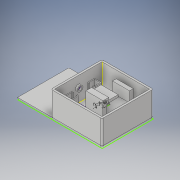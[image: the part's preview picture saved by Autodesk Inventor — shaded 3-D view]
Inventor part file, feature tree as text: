
AUTODESK INVENTOR PART (.ipt)
format: ipt  version: 2019 (Build 230136000, 136)  size: 371,712 bytes
history: native  units: in
note: dims shown in document units (in); Inventor stores cm internally (conversion verified against a paired STEP export)
features: extrude x25, sketch x22, fillet x2, other x1
ambient origin geometry x8: Origin, YZ Plane, XZ Plane, XY Plane, X Axis, Y Axis, Z Axis, Center Point
bodies: Solid1 (feature_tree)
feature tree (50):
  other  "ohisje"
  extrude  "Extrusion1"  Depth=1.9685in
  extrude  "Extrusion2"  Depth=0.0787in
  fillet  "Fillet1"  Radius=0.0787in
  sketch  "Sketch3"  dims[d5=0.0787in d6=1.378in]
  extrude  "Extrusion3"  Depth=1.378in
  sketch  "Sketch4"  dims[d7=2.126in d8=1.063in d9=0.0in d10=0.0787in]
  extrude  "Extrusion4"  Depth=1.063in TaperAngle=0.0deg
  fillet  "Fillet2"  Radius=0.0787in
  extrude  "Extrusion5"  Depth=0.0787in
  extrude  "Extrusion6"  Depth=0.315in
  extrude  "Extrusion7"  Depth=0.2402in
  sketch  "Sketch8"  dims[d30=0.0374in d31=0.0374in]
  extrude  "Extrusion8"  Depth=0.0374in
  extrude  "Extrusion9"  Depth=0.9843in
  extrude  "Extrusion10"  Depth=0.5906in TaperAngle=0.0deg
  extrude  "Extrusion11"  Depth=0.0394in
  extrude  "Extrusion12"  Depth=0.9843in
  sketch  "Sketch14"  dims[d46=0.1181in d47=1.2598in]
  extrude  "Extrusion13"  Depth=0.0394in TaperAngle=0.0deg
  extrude  "Extrusion14"  Depth=1.2598in
  extrude  "Extrusion16"  Depth=0.5512in TaperAngle=0.0deg
  extrude  "Extrusion17"  Depth=0.5512in TaperAngle=0.0deg
  extrude  "Extrusion18"  Depth=0.4724in
  extrude  "Extrusion19"  Depth=0.3937in TaperAngle=0.0deg
  extrude  "Extrusion20"  Depth=0.0374in
  extrude  "Extrusion21"  Depth=0.0374in
  sketch  "Sketch18"  dims[d54=0.5512in d55=0.4724in]
  sketch  "Sketch19"  dims[d56=0.0394in d57=0.3937in d58=0.0in]
  extrude  "Extrusion22"  Depth=0.0374in
  extrude  "Extrusion23"  Depth=0.2362in
  sketch  "Sketch20"  dims[d59=0.0374in d60=0.0374in]
  extrude  "Extrusion24"  Depth=0.0787in TaperAngle=0.0deg
  extrude  "Extrusion25"  Depth=0.3937in
  extrude  "Extrusion26"  Depth=0.1969in TaperAngle=0.0deg
  sketch  "Sketch1"  dims[d0=1.9685in d1=1.9685in]
  sketch  "Sketch2"  dims[d2=0.0787in d3=0.0787in d4=0.0787in]
  sketch  "Sketch5"  dims[d11=3.5039in d12=0.0in d13=0.0787in]
  sketch  "Sketch6"  dims[d26=0.3543in d27=0.315in]
  sketch  "Sketch7"  dims[d28=0.0394in d29=0.2402in]
  sketch  "Sketch9"  dims[d33=0.9843in d34=0.9843in]
  sketch  "Sketch10"  dims[d35=0.5906in d36=0.0in d37=0.5906in d38=0.0in]
  sketch  "Sketch11"  dims[d39=0.6299in d40=0.0394in]
  sketch  "Sketch12"  dims[d41=0.1417in d42=0.9843in]
  sketch  "Sketch13"  dims[d43=0.5512in d44=0.0394in d45=0.0in]
  sketch  "Sketch15"  dims[d48=0.0591in d49=0.5512in d50=0.0in]
  sketch  "Sketch17"  dims[d51=0.1417in d52=0.5512in d53=0.0in]
  sketch  "Sketch21"  dims[d61=0.3937in d62=0.0in d63=0.0374in]
  sketch  "Sketch22"  dims[d64=0.0374in d65=0.0374in]
  sketch  "Sketch23"  dims[d66=0.3937in d67=0.0in d68=0.2362in d69=0.0787in d70=0.0in d71=0.3937in d72=0.1969in d73=0.0in d74=0.8661in d75=0.7087in d76=0.7087in d77=0.3937in d78=0.7087in d79=0.3543in d80=0.0in d81=0.1575in d82=0.6299in d83=0.0in d87=0.1575in d88=0.7874in d89=0.0in d90=0.0787in d91=0.9449in d92=0.0in d93=0.2362in d94=0.0394in d95=0.0394in d96=0.1181in d97=0.1181in d98=0.0394in d99=0.0394in d100=0.3937in d101=0.0394in d102=0.0394in d103=0.9449in d104=0.0in d105=0.9449in d106=0.0in d107=0.9449in d108=0.0in d109=0.1969in d110=0.4724in d111=0.0in d112=0.3543in d113=0.1181in d114=0.1575in d115=0.1181in d116=0.1575in d117=0.3937in d118=0.0in d119=0.1181in d120=0.0in d121=0.1181in d122=0.1575in d123=0.0in d124=0.0787in d125=0.2756in d126=0.8268in d127=0.7874in d128=0.0in d129=0.0591in d130=0.0984in d131=0.3937in d132=0.0in]
